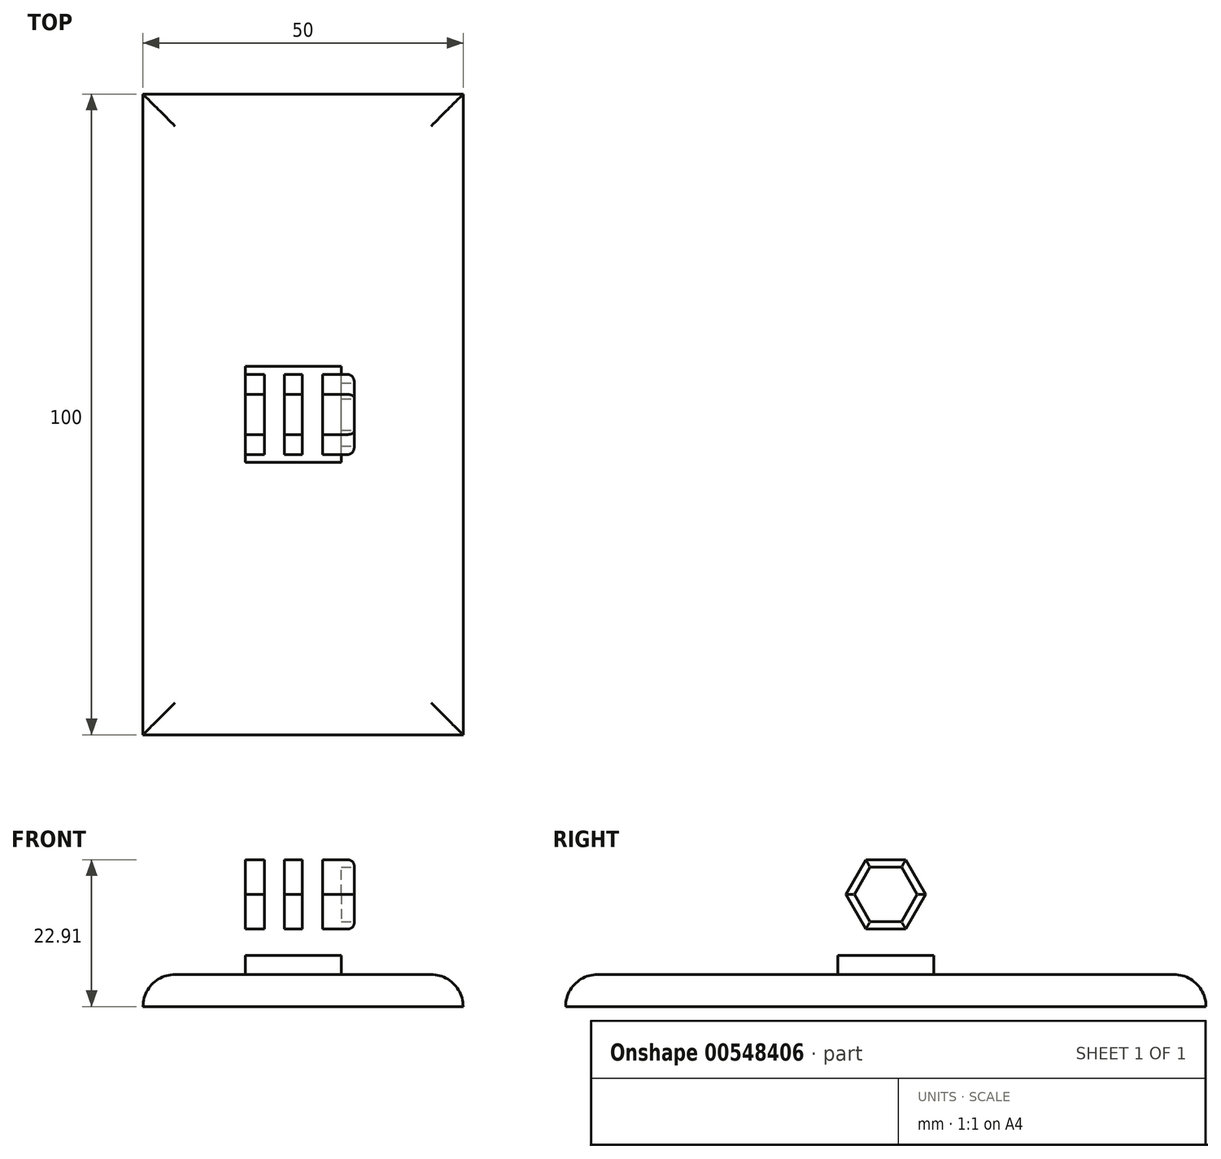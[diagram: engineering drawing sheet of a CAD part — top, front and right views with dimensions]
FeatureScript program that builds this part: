
annotation { "Feature Type Name" : "Feature", "Feature Type Description" : "" }
export const myFeature = defineFeature(function(context is Context, id is Id, definition is map)
    precondition{}
    {
        {
            var Q0;
            Q0=qCreatedBy(makeId("Right.planeOp"),FACE);
            var sketch = newSketch(context, id + "F0", { "sketchPlane" : qUnion([Q0])});
            skPoint(sketch, "E0", {"position": v(0, 12.5) * mm});
            skPoint(sketch, "E1", {"position": v(7.5, 0) * mm});
            skPoint(sketch, "E2.end.orphan", {"position": v(-7.5, 0) * mm});
            skLineSegment(sketch, "E3.top", {"start": v(-7.5, 0) * mm, "end": v(7.5, 0) * mm});
            skLineSegment(sketch, "E3.left", {"start": v(-7.5, 12.5) * mm, "end": v(-7.5, 0) * mm});
            skLineSegment(sketch, "E3.right", {"start": v(7.5, 12.5) * mm, "end": v(7.5, 0) * mm});
            skArc(sketch, "E4", {"start": v(7.5, 12.5) * mm, "mid": v(0, 20) * mm, "end": v(-7.5, 12.5) * mm});
            skCircle(sketch, "E5.cCircle", {"center": v(0, 12.5) * mm, "radius": 4.25 * mm, "construction": true});
            skLineSegment(sketch, "E5.0", {"start": v(-2.45, 16.75) * mm, "end": v(2.45, 16.75) * mm});
            skLineSegment(sketch, "E5.1", {"start": v(2.45, 16.75) * mm, "end": v(4.9, 12.5) * mm});
            skLineSegment(sketch, "E5.2", {"start": v(4.9, 12.5) * mm, "end": v(2.45, 8.25) * mm});
            skLineSegment(sketch, "E5.3", {"start": v(2.45, 8.25) * mm, "end": v(-2.45, 8.25) * mm});
            skLineSegment(sketch, "E5.4", {"start": v(-2.45, 8.25) * mm, "end": v(-4.9, 12.5) * mm});
            skLineSegment(sketch, "E5.5", {"start": v(-4.9, 12.5) * mm, "end": v(-2.45, 16.75) * mm});
            skPoint(sketch, "E5.0.midPoint", {"position": v(0, 16.75) * mm});
            skCircle(sketch, "E6.cCircle", {"center": v(0, 12.5) * mm, "radius": 5.41 * mm, "construction": true});
            skLineSegment(sketch, "E6.0", {"start": v(-3.12, 17.91) * mm, "end": v(3.12, 17.91) * mm});
            skLineSegment(sketch, "E6.1", {"start": v(3.12, 17.91) * mm, "end": v(6.25, 12.5) * mm});
            skLineSegment(sketch, "E6.2", {"start": v(6.25, 12.5) * mm, "end": v(3.12, 7.09) * mm});
            skLineSegment(sketch, "E6.3", {"start": v(3.13, 7.09) * mm, "end": v(-3.12, 7.09) * mm});
            skLineSegment(sketch, "E6.4", {"start": v(-3.12, 7.09) * mm, "end": v(-6.25, 12.5) * mm});
            skLineSegment(sketch, "E6.5", {"start": v(-6.25, 12.5) * mm, "end": v(-3.12, 17.91) * mm});
            skPoint(sketch, "E6.0.midPoint", {"position": v(0, 17.91) * mm});
            skLineSegment(sketch, "E7.top", {"start": v(-7.5, 3) * mm, "end": v(7.5, 3) * mm});
            skLineSegment(sketch, "E7.left", {"start": v(-7.5, 0) * mm, "end": v(-7.5, 3) * mm});
            skLineSegment(sketch, "E7.right", {"start": v(7.5, 0) * mm, "end": v(7.5, 3) * mm});
            skSolve(sketch);
        }
        {
            var Q0;
            Q0=makeQuery(id+"F0.imprint","IMPRINT",FACE,{"disambiguationData":[TD([[makeQuery(id+"F0.imprint","IMPRINT",EDGE,{"derivedFrom":sQuery(id+"F0.wireOp",EDGE,"E3.top")}),1.0]])]});
            extrude(context, id + "F1", {"entities" : qUnion([Q0]), "oppositeDirection" : true, "depth" : 15 * mm});
        }
        {
            var Q0;
            Q0=makeQuery(id+"F0.imprint","IMPRINT",FACE,{"disambiguationData":[TD([[makeQuery(id+"F0.imprint","IMPRINT",EDGE,{"derivedFrom":sQuery(id+"F0.wireOp",EDGE,"E3.left")}),1.0]])]});
            extrude(context, id + "F2", {"entities" : qUnion([Q0]), "operationType" : NewBodyOperationType.ADD, "oppositeDirection" : true, "depth" : 3 * mm});
        }
        {
            var Q0;
            Q0=makeQuery(id+"F0.imprint","IMPRINT",FACE,{"disambiguationData":[TD([[makeQuery(id+"F0.imprint","IMPRINT",EDGE,{"derivedFrom":sQuery(id+"F0.wireOp",EDGE,"E5.0")}),1.0]])]});
            extrude(context, id + "F3", {"entities" : qUnion([Q0]), "operationType" : NewBodyOperationType.ADD, "oppositeDirection" : true, "depth" : 3 * mm});
        }
        {
            var Q0;
            Q0=makeQuery(id+"F0.imprint","IMPRINT",FACE,{"disambiguationData":[TD([[makeQuery(id+"F0.imprint","IMPRINT",EDGE,{"derivedFrom":sQuery(id+"F0.wireOp",EDGE,"E5.0")}),1.0]])]});
            extrude(context, id + "F4", {"entities" : qUnion([Q0]), "operationType" : NewBodyOperationType.ADD, "depth" : 2 * mm});
        }
        {
            var Q0;
            Q0=makeQuery(id+"F0.imprint","IMPRINT",FACE,{"disambiguationData":[TD([[makeQuery(id+"F0.imprint","IMPRINT",EDGE,{"derivedFrom":sQuery(id+"F0.wireOp",EDGE,"E5.0")}),-1.0]])]});
            extrude(context, id + "F5", {"entities" : qUnion([Q0]), "operationType" : NewBodyOperationType.ADD, "oppositeDirection" : true, "depth" : 3 * mm});
        }
        {
            var Q0;
            {var subQ0=sQuery(id+"F0.wireOp",EDGE,"E5.5");var subQ1=sQuery(id+"F0.wireOp",EDGE,"E5.4");var subQ2=sQuery(id+"F0.wireOp",EDGE,"E5.3");var subQ3=sQuery(id+"F0.wireOp",EDGE,"E5.2");var subQ4=sQuery(id+"F0.wireOp",EDGE,"E5.1");var subQ5=sQuery(id+"F0.wireOp",EDGE,"E5.0");var subQ6=sQuery(id+"F0.wireOp",EDGE,"E6.5");var subQ7=sQuery(id+"F0.wireOp",EDGE,"E6.4");var subQ8=sQuery(id+"F0.wireOp",EDGE,"E6.3");var subQ9=sQuery(id+"F0.wireOp",EDGE,"E6.2");var subQ10=sQuery(id+"F0.wireOp",EDGE,"E6.1");var subQ11=sQuery(id+"F0.wireOp",EDGE,"E6.0");Q0=makeQuery(id+"F5.boolean.opBoolean","MERGE",FACE,{"derivedFrom":[makeQuery(id+"F3.boolean.opBoolean","MERGE",FACE,{"derivedFrom":[makeQuery(id+"F2.opExtrude","CAP_FACE",FACE,{"disambiguationData":[OSD([sQuery(id+"F0.wireOp",EDGE,"E3.left"),sQuery(id+"F0.wireOp",EDGE,"E3.right"),sQuery(id+"F0.wireOp",EDGE,"E4"),subQ11,subQ10,subQ9,subQ8,subQ7,subQ6,sQuery(id+"F0.wireOp",EDGE,"E7.top")])],"isStart":false}),makeQuery(id+"F3.opExtrude","CAP_FACE",FACE,{"disambiguationData":[OSD([subQ5,subQ4,subQ3,subQ2,subQ1,subQ0,subQ11,subQ10,subQ9,subQ8,subQ7,subQ6])],"isStart":false})]}),makeQuery(id+"F5.opExtrude","CAP_FACE",FACE,{"disambiguationData":[OSD([subQ5,subQ4,subQ3,subQ2,subQ1,subQ0])],"isStart":false})]});}
            extrude(context, id + "F6", {"entities" : qUnion([Q0]), "operationType" : NewBodyOperationType.ADD, "depth" : 12 * mm});
        }
        {
            var Q0;
            Q0=sQuery(id+"F0.wireOp",VERTEX,"E0");
            var Q1;
            Q1=makeQuery(id+"F1.opExtrude","SWEPT_BODY",BODY,{"disambiguationData":[OSD([sQuery(id+"F0.wireOp",EDGE,"E3.top"),sQuery(id+"F0.wireOp",EDGE,"E7.top"),sQuery(id+"F0.wireOp",EDGE,"E7.left"),sQuery(id+"F0.wireOp",EDGE,"E7.right")])]});
            hole(context, id + "F7", {"style" : HoleStyle.SIMPLE, "endStyle" : HoleEndStyle.BLIND, "holeDiameter" : 5 * mm, "holeDepth" : 15 * mm, "locations" : qUnion([Q0]), "scope" : qUnion([Q1])});
        }
        {
            var Q0;
            Q0=qCreatedBy(makeId("Top.planeOp"),FACE);
            cPlane(context, id + "F8", {"entities" : qUnion([Q0]), "cplaneType" : CPlaneType.OFFSET, "offset" : 20 * mm, "width" : 150 * mm, "height" : 150 * mm});
        }
        {
            var Q0;
            Q0=qCreatedBy(id+"F8.planeOp",FACE);
            var sketch = newSketch(context, id + "F9", { "sketchPlane" : qUnion([Q0])});
            skLineSegment(sketch, "E8.top", {"start": v(0, 7.5) * mm, "end": v(-15, 7.5) * mm});
            skLineSegment(sketch, "E8.left", {"start": v(0, 0) * mm, "end": v(0, 7.5) * mm});
            skLineSegment(sketch, "E8.right", {"start": v(-15, 0) * mm, "end": v(-15, 7.5) * mm});
            skLineSegment(sketch, "E9.top", {"start": v(-15, -7.5) * mm, "end": v(0, -7.5) * mm});
            skLineSegment(sketch, "E9.left", {"start": v(-15, 0) * mm, "end": v(-15, -7.5) * mm});
            skLineSegment(sketch, "E9.right", {"start": v(0, 0) * mm, "end": v(0, -7.5) * mm});
            skLineSegment(sketch, "E10", {"start": v(-7.5, -7.5) * mm, "end": v(-7.5, 7.5) * mm, "construction": true});
            skPoint(sketch, "E11", {"position": v(-6.1, -7.5) * mm});
            skLineSegment(sketch, "E12.bottom", {"start": v(-6.1, -7.5) * mm, "end": v(-8.9, -7.5) * mm});
            skLineSegment(sketch, "E12.top", {"start": v(-6.1, 7.5) * mm, "end": v(-8.9, 7.5) * mm});
            skLineSegment(sketch, "E12.left", {"start": v(-6.1, -7.5) * mm, "end": v(-6.1, 7.5) * mm});
            skLineSegment(sketch, "E12.right", {"start": v(-8.9, -7.5) * mm, "end": v(-8.9, 7.5) * mm});
            skLineSegment(sketch, "E13.bottom", {"start": v(-15, -7.5) * mm, "end": v(-12.05, -7.5) * mm});
            skLineSegment(sketch, "E13.top", {"start": v(-15, 7.5) * mm, "end": v(-12.05, 7.5) * mm});
            skLineSegment(sketch, "E13.left", {"start": v(-15, -7.5) * mm, "end": v(-15, 7.5) * mm});
            skLineSegment(sketch, "E13.right", {"start": v(-12.05, -7.5) * mm, "end": v(-12.05, 7.5) * mm});
            skLineSegment(sketch, "E14.bottom", {"start": v(0, -7.5) * mm, "end": v(-2.95, -7.5) * mm});
            skLineSegment(sketch, "E14.top", {"start": v(0, 7.5) * mm, "end": v(-2.95, 7.5) * mm});
            skLineSegment(sketch, "E14.left", {"start": v(0, -7.5) * mm, "end": v(0, 7.5) * mm});
            skLineSegment(sketch, "E14.right", {"start": v(-2.95, -7.5) * mm, "end": v(-2.95, 7.5) * mm});
            skSolve(sketch);
        }
        {
            var Q0;
            {var subQ2=sQuery(id+"F9.wireOp",EDGE,"E12.right");Q0=makeQuery(id+"F9.imprint","IMPRINT",FACE,{"disambiguationData":[TD([[makeQuery(id+"F9.imprint","IMPRINT",EDGE,{"derivedFrom":subQ2}),1.0]])]});}
            var Q1;
            {var subQ2=sQuery(id+"F9.wireOp",EDGE,"E12.left");Q1=makeQuery(id+"F9.imprint","IMPRINT",FACE,{"disambiguationData":[TD([[makeQuery(id+"F9.imprint","IMPRINT",EDGE,{"derivedFrom":subQ2}),-1.0]])]});}
            extrude(context, id + "F10", {"entities" : qUnion([Q0, Q1]), "operationType" : NewBodyOperationType.REMOVE, "oppositeDirection" : true, "depth" : 17 * mm});
        }
        {
            var Q0;
            Q0=makeQuery(id+"F4.opExtrude","CAP_EDGE",EDGE,{"disambiguationData":[OSD([sQuery(id+"F0.wireOp",EDGE,"E6.4")])],"isStart":false});
            var Q1;
            Q1=makeQuery(id+"F4.opExtrude","CAP_EDGE",EDGE,{"disambiguationData":[OSD([sQuery(id+"F0.wireOp",EDGE,"E6.3")])],"isStart":false});
            var Q2;
            Q2=makeQuery(id+"F4.opExtrude","CAP_EDGE",EDGE,{"disambiguationData":[OSD([sQuery(id+"F0.wireOp",EDGE,"E6.5")])],"isStart":false});
            var Q3;
            Q3=makeQuery(id+"F4.opExtrude","CAP_EDGE",EDGE,{"disambiguationData":[OSD([sQuery(id+"F0.wireOp",EDGE,"E6.0")])],"isStart":false});
            var Q4;
            Q4=makeQuery(id+"F4.opExtrude","CAP_EDGE",EDGE,{"disambiguationData":[OSD([sQuery(id+"F0.wireOp",EDGE,"E6.1")])],"isStart":false});
            var Q5;
            Q5=makeQuery(id+"F4.opExtrude","CAP_EDGE",EDGE,{"disambiguationData":[OSD([sQuery(id+"F0.wireOp",EDGE,"E6.2")])],"isStart":false});
            fillet(context, id + "F11", {"entities" : qUnion([Q0, Q1, Q2, Q3, Q4, Q5]), "radius" : 1 * mm, "tangentPropagation" : true, "allowEdgeOverflow" : false});
        }
        {
            var Q0;
            Q0=qCreatedBy(makeId("Top.planeOp"),FACE);
            var sketch = newSketch(context, id + "F12", { "sketchPlane" : qUnion([Q0])});
            skLineSegment(sketch, "E15.bottom", {"start": v(-31, -50) * mm, "end": v(19, -50) * mm});
            skLineSegment(sketch, "E15.top", {"start": v(-31, 50) * mm, "end": v(19, 50) * mm});
            skLineSegment(sketch, "E15.left", {"start": v(-31, -50) * mm, "end": v(-31, 50) * mm});
            skLineSegment(sketch, "E15.right", {"start": v(19, -50) * mm, "end": v(19, 50) * mm});
            skPoint(sketch, "E15.middle", {"position": v(-6, 0) * mm});
            skSolve(sketch);
        }
        {
            var Q0;
            Q0 = qSketchRegion(id + "F12", true);
            extrude(context, id + "F13", {"entities" : qUnion([Q0]), "operationType" : NewBodyOperationType.ADD, "oppositeDirection" : true, "depth" : 5 * mm, "offsetDistance" : 25 * mm});
        }
        {
            var Q0;
            Q0=makeQuery(id+"F13.opExtrude","CAP_EDGE",EDGE,{"disambiguationData":[OSD([sQuery(id+"F12.wireOp",EDGE,"E15.top")])],"isStart":true});
            var Q1;
            Q1=makeQuery(id+"F13.opExtrude","CAP_EDGE",EDGE,{"disambiguationData":[OSD([sQuery(id+"F12.wireOp",EDGE,"E15.right")])],"isStart":true});
            var Q2;
            Q2=makeQuery(id+"F13.opExtrude","CAP_EDGE",EDGE,{"disambiguationData":[OSD([sQuery(id+"F12.wireOp",EDGE,"E15.bottom")])],"isStart":true});
            var Q3;
            Q3=makeQuery(id+"F13.opExtrude","CAP_EDGE",EDGE,{"disambiguationData":[OSD([sQuery(id+"F12.wireOp",EDGE,"E15.left")])],"isStart":true});
            fillet(context, id + "F14", {"entities" : qUnion([Q0, Q1, Q2, Q3]), "radius" : 5 * mm, "tangentPropagation" : true, "allowEdgeOverflow" : false});
        }
    });
